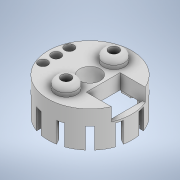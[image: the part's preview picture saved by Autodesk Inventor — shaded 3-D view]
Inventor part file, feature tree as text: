
AUTODESK INVENTOR PART (.ipt)
format: ipt  version: 2020.4 (Build 244396010, 396A)  size: 285,184 bytes
history: native  units: mm
features: extrude x7, sketch x7, mirror x1, pattern_circular x1, fillet x1
ambient origin geometry x8: Origin, YZ Plane, XZ Plane, XY Plane, X Axis, Y Axis, Z Axis, Center Point
bodies: Solid1 (feature_tree)
feature tree (17):
  extrude  "Extrusion1"  Depth=8.0mm TaperAngle=0.0deg
  extrude  "Extrusion2"  Depth=12.7mm
  extrude  "Extrusion3"  Depth=12.7mm
  mirror  "Mirror1"
  extrude  "Extrusion5"  Depth=3.0mm
  pattern_circular  "Circular Pattern1"  Angle=180.0deg  [1 undecoded]
  fillet  "Fillet1"  [1 undecoded]
  extrude  "Extrusion6"  TaperAngle=60.0deg  [1 undecoded]
  extrude  "Extrusion7"  Depth=11.0mm TaperAngle=0.0deg
  extrude  "Extrusion8"  Depth=7.0mm TaperAngle=360.0deg
  sketch  "Sketch1"  dims[d0=44.5mm d1=8.0mm d2=0.0mm]
  sketch  "Sketch2"  dims[d3=5.2mm d4=12.7mm]
  sketch  "Sketch3"  dims[d5=5.2mm d6=12.7mm]
  sketch  "Sketch4"  dims[d7=5.0mm d8=0.0mm d9=3.0mm]
  sketch  "Sketch6"  dims[d10=5.0mm d11=0.0mm]
  sketch  "Sketch7"  dims[d17=3.0mm]
  sketch  "Sketch9"  dims[d18=5.0mm d19=180.0deg d20=120.0deg d21=60.0deg d22=11.0mm d23=0.0mm d24=120.0mm d25=360.0deg d27=3.0mm d29=18.0mm d30=90.0deg d32=7.0mm d33=0.0mm d34=3.0mm d35=5.0mm d36=4.0mm d37=30.0mm d39=7.0mm d40=10.0mm d42=10.0mm d44=11.0mm d45=5.0mm d46=30.0mm d48=7.0mm d49=10.0mm d51=10.0mm d53=21.0mm d54=10.0mm d55=0.0mm d56=7.0mm d57=7.0mm d58=0.0mm d59=0.5mm d60=0.872665mm]
note: 3 required parameter values undecoded (feature->parameter linkage not recoverable at this tier; creation-order binding heuristic only, values carry confidence <= 0.55)
